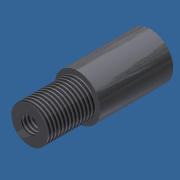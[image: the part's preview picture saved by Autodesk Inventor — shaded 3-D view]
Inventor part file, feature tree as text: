
AUTODESK INVENTOR PART (.ipt)
format: ipt  version: 2012 (Build 160160000, 160)  size: 97,280 bytes
history: native  units: in
note: dims shown in document units (in); Inventor stores cm internally (conversion verified against a paired STEP export)
features: extrude x3, sketch x2, thread x2
ambient origin geometry x8: Origin, YZ Plane, XZ Plane, XY Plane, X Axis, Y Axis, Z Axis, Center Point
bodies: Solid1 (feature_tree)
feature tree (7):
  sketch  "Sketch1"  dims[d0=0.625in d1=0.5in]
  extrude  "Extrusion1"  Depth=0.5in
  extrude  "Extrusion2"  Depth=0.66in TaperAngle=0.0deg
  thread  "Thread1"  [1 undecoded]
  extrude  "Extrusion3"  Depth=0.23in
  thread  "Thread2"  [1 undecoded]
  sketch  "Sketch2"  dims[d2=1.0in d3=0.0in d4=0.66in d5=0.0in d6=1.0in d7=0.0in d8=0.23in d9=1.0in d10=0.0in d11=1.0in d12=0.0in]
note: 2 required parameter values undecoded (feature->parameter linkage not recoverable at this tier; creation-order binding heuristic only, values carry confidence <= 0.55)
